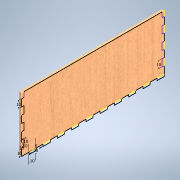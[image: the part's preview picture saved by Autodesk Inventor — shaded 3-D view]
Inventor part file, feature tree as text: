
AUTODESK INVENTOR PART (.ipt)
format: ipt  version: 2021 (Build 250183000, 183)  size: 229,376 bytes
history: native  units: mm
features: extrude x3, sketch x3, other x1
ambient origin geometry x8: Origin, YZ Plane, XZ Plane, XY Plane, X Axis, Y Axis, Z Axis, Center Point
bodies: Solid1 (feature_tree)
feature tree (7):
  other  "DoosjeRechterkant"
  extrude  "Extrusion1"  Depth=200.0mm
  extrude  "Extrusion2"  Depth=10.0mm
  extrude  "Extrusion3"  Depth=10.0mm
  sketch  "Sketch1"  dims[d0=77.0mm d1=200.0mm]
  sketch  "Sketch2"  dims[d2=3.0mm d3=0.0mm d4=10.0mm]
  sketch  "Sketch3"  dims[d5=3.0mm d6=10.0mm d7=100.0mm d9=20.0mm d10=10.0mm d12=10.0mm d14=10.0mm d15=3.0mm d16=10.0mm d17=30.0mm d19=20.0mm d20=10.0mm d22=10.0mm d24=10.0mm d25=10.0mm d26=3.0mm d27=0.0mm d28=10.0mm d29=3.0mm d30=10.0mm d31=20.0mm d32=3.0mm d33=0.0mm]
